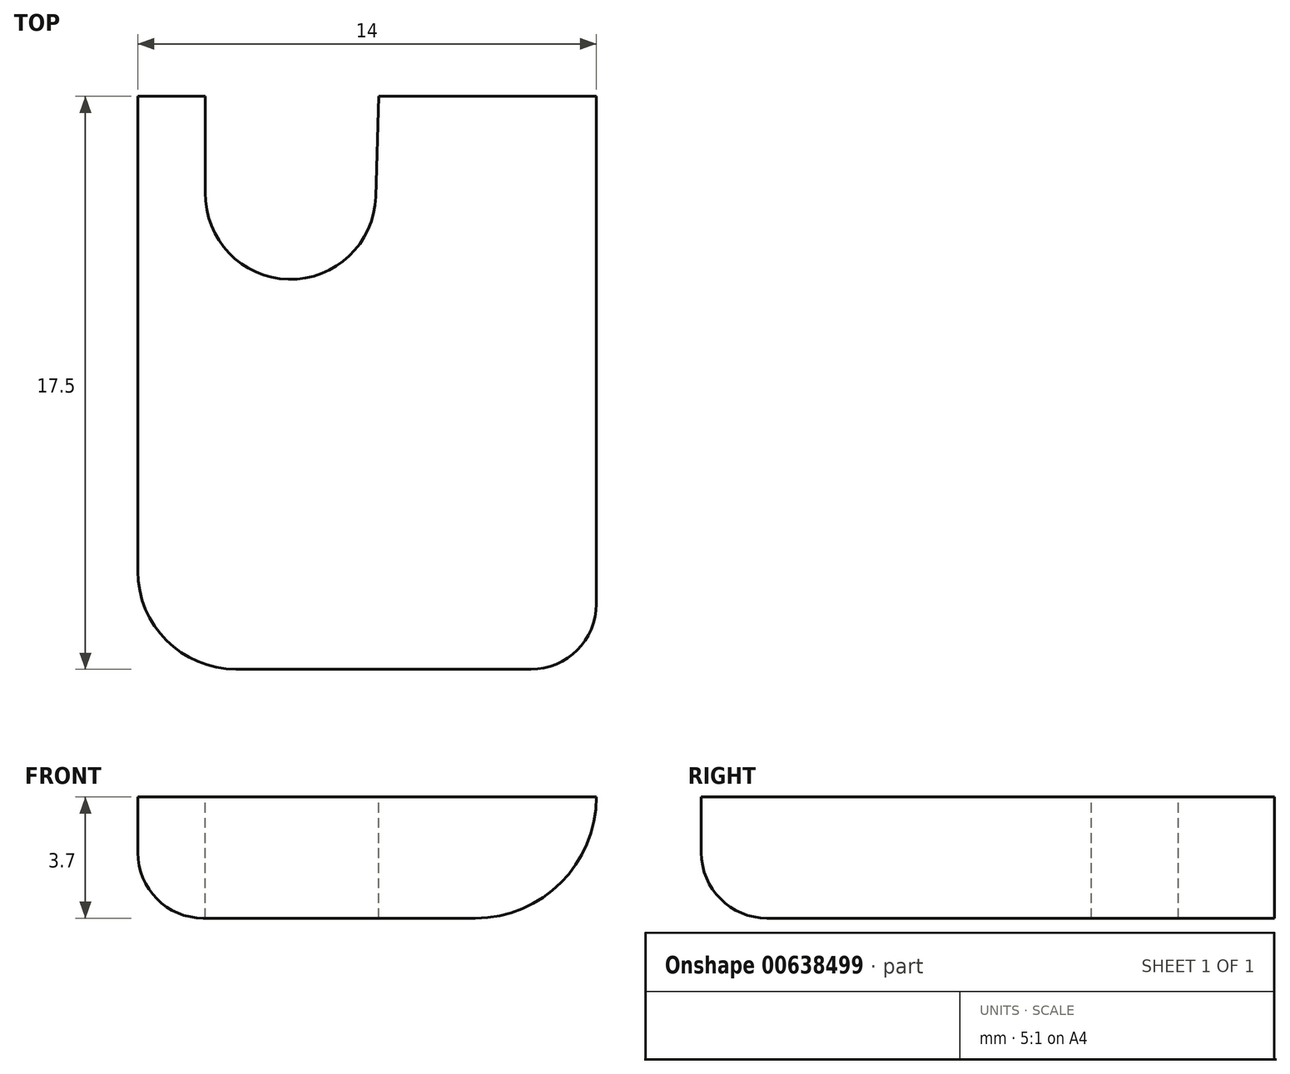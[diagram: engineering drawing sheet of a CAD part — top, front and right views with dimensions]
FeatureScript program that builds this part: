
annotation { "Feature Type Name" : "Feature", "Feature Type Description" : "" }
export const myFeature = defineFeature(function(context is Context, id is Id, definition is map)
    precondition{}
    {
        {
            var Q0;
            Q0=qCreatedBy(makeId("Top.planeOp"),FACE);
            var sketch = newSketch(context, id + "F0", { "sketchPlane" : qUnion([Q0])});
            skLineSegment(sketch, "E0.bottom", {"start": v(-7.41, 12.17) * mm, "end": v(6.59, 12.17) * mm});
            skLineSegment(sketch, "E0.top", {"start": v(-7.41, -5.33) * mm, "end": v(6.59, -5.33) * mm});
            skLineSegment(sketch, "E0.left", {"start": v(-7.41, 12.17) * mm, "end": v(-7.41, -5.33) * mm});
            skLineSegment(sketch, "E0.right", {"start": v(6.59, 12.17) * mm, "end": v(6.59, -5.33) * mm});
            skSolve(sketch);
        }
        {
            var Q0;
            Q0=qSketchRegion(id+"F0",true);
            extrude(context, id + "F1", {"entities" : qUnion([Q0]), "depth" : 3.7 * mm, "offsetDistance" : 25 * mm});
        }
        {
            var Q0;
            Q0=makeQuery(id+"F1.opExtrude","CAP_FACE",FACE,{"disambiguationData":[OSD([sQuery(id+"F0.wireOp",EDGE,"E0.bottom"),sQuery(id+"F0.wireOp",EDGE,"E0.top"),sQuery(id+"F0.wireOp",EDGE,"E0.left"),sQuery(id+"F0.wireOp",EDGE,"E0.right")])],"isStart":false});
            var sketch = newSketch(context, id + "F2", { "sketchPlane" : qUnion([Q0])});
            skArc(sketch, "E1", {"start": v(-5.35, 9.23) * mm, "mid": v(-2.8, 6.58) * mm, "end": v(-0.15, 9.1) * mm});
            skLineSegment(sketch, "E2", {"start": v(-0.15, 9.1) * mm, "end": v(-0.06, 12.17) * mm});
            skLineSegment(sketch, "E3", {"start": v(-5.35, 9.13) * mm, "end": v(-5.35, 12.17) * mm});
            skSolve(sketch);
        }
        {
            var Q0;
            Q0=qSketchRegion(id+"F2",true);
            var Q1;
            {var subQ0=sQuery(id+"F2.wireOp",EDGE,"E2");Q1=makeQuery(id+"F2.imprint","IMPRINT",FACE,{"disambiguationData":[TD([[makeQuery(id+"F2.imprint","IMPRINT",EDGE,{"derivedFrom":subQ0}),1.0]])]});}
            extrude(context, id + "F3", {"entities" : qUnion([Q0, Q1]), "operationType" : NewBodyOperationType.REMOVE, "oppositeDirection" : true, "depth" : 5.4 * mm, "offsetDistance" : 25 * mm});
        }
        {
            var Q0;
            Q0=makeQuery(id+"F1.opExtrude","CAP_EDGE",EDGE,{"disambiguationData":[OSD([sQuery(id+"F0.wireOp",EDGE,"E0.right")])],"isStart":true});
            fillet(context, id + "F4", {"entities" : qUnion([Q0]), "radius" : 3.7 * mm, "tangentPropagation" : true, "allowEdgeOverflow" : false});
        }
        {
            var Q0;
            Q0=makeQuery(id+"F1.opExtrude","SWEPT_EDGE",EDGE,{"disambiguationData":[OSD([sQuery(id+"F0.wireOp",EDGE,"E0.top"),sQuery(id+"F0.wireOp",EDGE,"E0.left")])]});
            fillet(context, id + "F5", {"entities" : qUnion([Q0]), "radius" : 3 * mm, "tangentPropagation" : true, "allowEdgeOverflow" : false});
        }
        {
            var Q0;
            Q0=makeQuery(id+"F4.opFillet","BLEND_EDGE",EDGE,{"blendedFrom":[makeQuery(id+"F1.opExtrude","CAP_EDGE",EDGE,{"disambiguationData":[OSD([sQuery(id+"F0.wireOp",EDGE,"E0.right")])],"isStart":true}),makeQuery(id+"F1.opExtrude","SWEPT_FACE",FACE,{"disambiguationData":[OSD([sQuery(id+"F0.wireOp",EDGE,"E0.top")])]})],"blendedInto":[makeQuery(id+"F1.opExtrude","SWEPT_FACE",FACE,{"disambiguationData":[OSD([sQuery(id+"F0.wireOp",EDGE,"E0.top")])]})]});
            fillet(context, id + "F6", {"entities" : qUnion([Q0]), "radius" : 2 * mm, "tangentPropagation" : true, "allowEdgeOverflow" : false});
        }
    });
